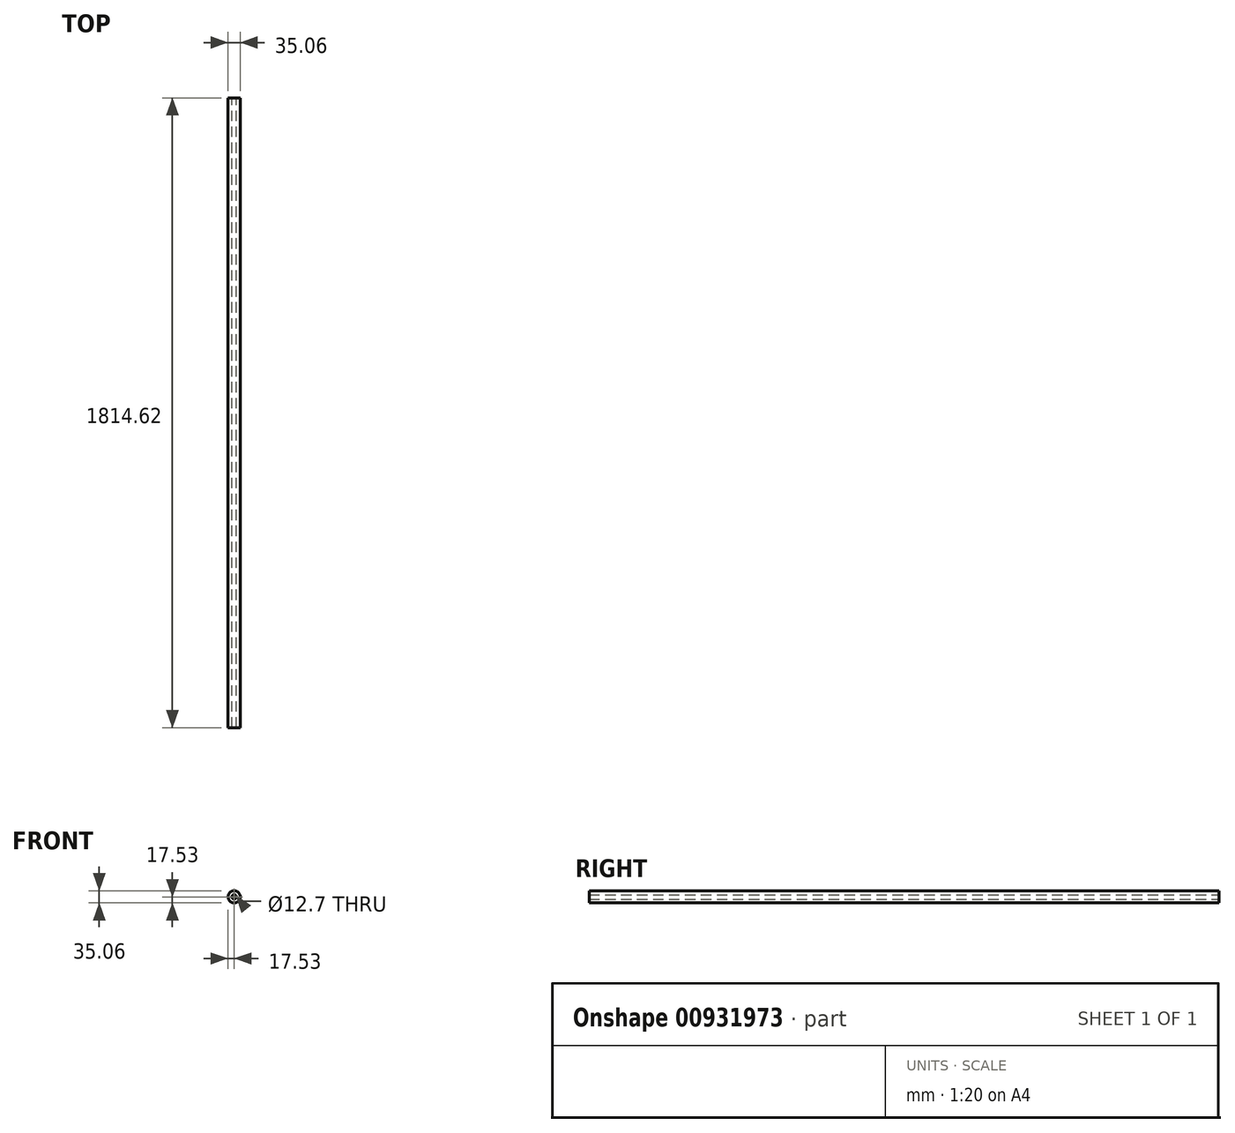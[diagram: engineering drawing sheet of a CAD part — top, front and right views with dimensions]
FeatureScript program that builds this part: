
annotation { "Feature Type Name" : "Feature", "Feature Type Description" : "" }
export const myFeature = defineFeature(function(context is Context, id is Id, definition is map)
    precondition{}
    {
        {
            assignVariable(context, id + "F0", {"name" : "StrutLength", "anyValue" : 1814.62 * mm});
        }
        {
            var Q0;
            Q0=qCreatedBy(makeId("Front.planeOp"),FACE);
            var sketch = newSketch(context, id + "F1", { "sketchPlane" : qUnion([Q0])});
            skCircle(sketch, "E0", {"center": v(0, 0) * mm, "radius": 6.35 * mm});
            skCircle(sketch, "E1", {"center": v(0, 0) * mm, "radius": 17.53 * mm});
            skSolve(sketch);
        }
        {
            var Q0;
            Q0=makeQuery(id+"F1.imprint","IMPRINT",FACE,{"disambiguationData":[TD([[makeQuery(id+"F1.imprint","IMPRINT",EDGE,{"derivedFrom":sQuery(id+"F1.wireOp",EDGE,"E0")}),-1.0]])]});
            extrude(context, id + "F2", {"entities" : qUnion([Q0]), "depth" : getVariable(context, 'StrutLength'), "offsetDistance" : 25.4 * mm});
        }
    });
